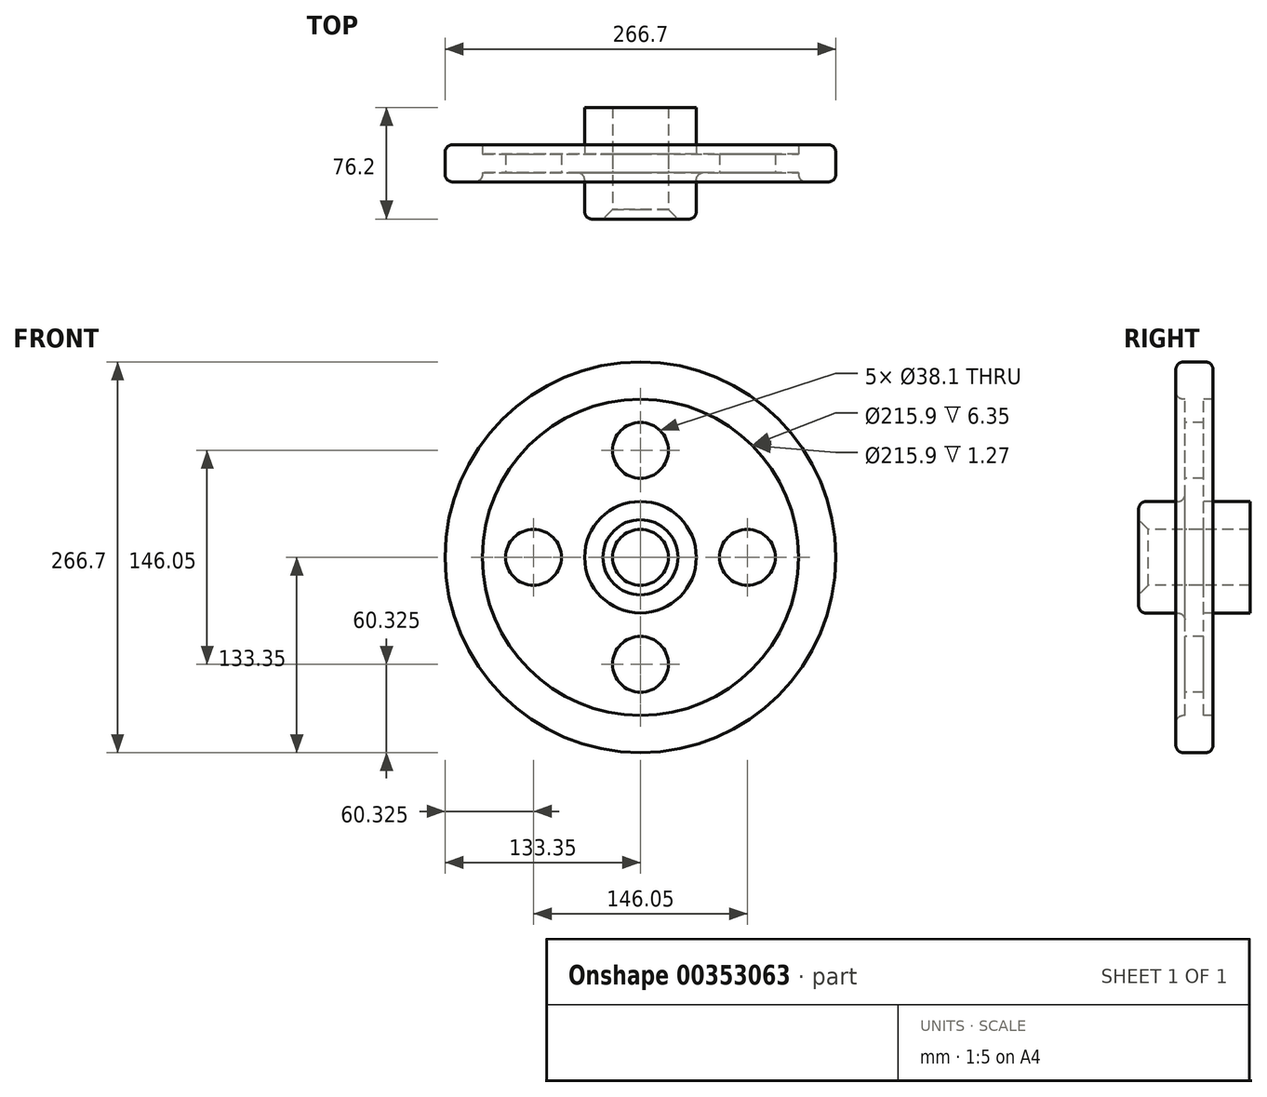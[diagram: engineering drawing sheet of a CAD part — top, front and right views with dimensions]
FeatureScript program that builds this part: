
annotation { "Feature Type Name" : "Feature", "Feature Type Description" : "" }
export const myFeature = defineFeature(function(context is Context, id is Id, definition is map)
    precondition{}
    {
        {
            var Q0;
            Q0=qCreatedBy(makeId("Right.planeOp"),FACE);
            var sketch = newSketch(context, id + "F0", { "sketchPlane" : qUnion([Q0])});
            skLineSegment(sketch, "E0", {"start": v(0, 0) * mm, "end": v(228.48, 0) * mm, "construction": true});
            skLineSegment(sketch, "E1", {"start": v(0, 0) * mm, "end": v(0, 368.94) * mm, "construction": true});
            skLineSegment(sketch, "E2.0", {"start": v(38.1, 19.05) * mm, "end": v(38.1, 38.1) * mm});
            skLineSegment(sketch, "E3.0", {"start": v(0, 19.05) * mm, "end": v(38.1, 19.05) * mm});
            skLineSegment(sketch, "E4.0", {"start": v(6.35, 38.1) * mm, "end": v(38.1, 38.1) * mm});
            skLineSegment(sketch, "E5.0", {"start": v(6.35, 107.95) * mm, "end": v(12.7, 107.95) * mm});
            skLineSegment(sketch, "E6.0", {"start": v(0, 133.35) * mm, "end": v(12.7, 133.35) * mm});
            skLineSegment(sketch, "E7.trimOffspring", {"start": v(12.7, 107.95) * mm, "end": v(12.7, 133.35) * mm});
            skLineSegment(sketch, "E8.trimOffspring", {"start": v(6.35, 38.1) * mm, "end": v(6.35, 107.95) * mm});
            skLineSegment(sketch, "E9.MirrorCS", {"start": v(0, 133.35) * mm, "end": v(-12.7, 133.35) * mm});
            skLineSegment(sketch, "E10.MirrorCS", {"start": v(-12.7, 107.95) * mm, "end": v(-12.7, 133.35) * mm});
            skLineSegment(sketch, "E11.MirrorCS", {"start": v(-6.35, 107.95) * mm, "end": v(-12.7, 107.95) * mm});
            skLineSegment(sketch, "E12.MirrorCS", {"start": v(-6.35, 38.1) * mm, "end": v(-6.35, 107.95) * mm});
            skLineSegment(sketch, "E13.MirrorCS", {"start": v(-6.35, 38.1) * mm, "end": v(-38.1, 38.1) * mm});
            skLineSegment(sketch, "E14.MirrorCS", {"start": v(0, 19.05) * mm, "end": v(-38.1, 19.05) * mm});
            skLineSegment(sketch, "E15.MirrorCS", {"start": v(-38.1, 19.05) * mm, "end": v(-38.1, 38.1) * mm});
            skSolve(sketch);
        }
        {
            var Q0;
            Q0=makeQuery(id+"F0.imprint","IMPRINT",FACE,{"disambiguationData":[TD([[makeQuery(id+"F0.imprint","IMPRINT",EDGE,{"derivedFrom":sQuery(id+"F0.wireOp",EDGE,"E2.0")}),1.0]])]});
            var Q1;
            Q1=sQuery(id+"F0.wireOp",EDGE,"E0");
            revolve(context, id + "F1", {"entities" : qUnion([Q0]), "axis" : qUnion([Q1]), "revolveType" : RevolveType.FULL});
        }
        {
            var Q0;
            Q0=makeQuery(id+"F1.opRevolve","SWEPT_FACE",FACE,{"disambiguationData":[OSD([sQuery(id+"F0.wireOp",EDGE,"E12.MirrorCS")])]});
            var sketch = newSketch(context, id + "F2", { "sketchPlane" : qUnion([Q0])});
            skLineSegment(sketch, "E16", {"start": v(0, 0) * mm, "end": v(0, 73.03) * mm});
            skCircle(sketch, "E17", {"center": v(0, 73.03) * mm, "radius": 19.05 * mm});
            skCircle(sketch, "E18.1.0", {"center": v(-73.03, 0) * mm, "radius": 19.05 * mm});
            skCircle(sketch, "E18.2.0", {"center": v(0, -73.03) * mm, "radius": 19.05 * mm});
            skCircle(sketch, "E18.3.0", {"center": v(73.03, 0) * mm, "radius": 19.05 * mm});
            skPoint(sketch, "E18.center", {"position": v(0, 0) * mm});
            skSolve(sketch);
        }
        {
            var Q0;
            Q0=makeQuery(id+"F2.imprint","IMPRINT",FACE,{"disambiguationData":[TD([[makeQuery(id+"F2.imprint","IMPRINT",EDGE,{"derivedFrom":sQuery(id+"F2.wireOp",EDGE,"E18.2.0")}),1.0]])]});
            var Q1;
            Q1=makeQuery(id+"F2.imprint","IMPRINT",FACE,{"disambiguationData":[TD([[makeQuery(id+"F2.imprint","IMPRINT",EDGE,{"derivedFrom":sQuery(id+"F2.wireOp",EDGE,"E18.3.0")}),1.0]])]});
            var Q2;
            Q2=makeQuery(id+"F2.imprint","IMPRINT",FACE,{"disambiguationData":[TD([[makeQuery(id+"F2.imprint","IMPRINT",EDGE,{"derivedFrom":sQuery(id+"F2.wireOp",EDGE,"E18.1.0")}),1.0]])]});
            var Q3;
            Q3=makeQuery(id+"F2.imprint","IMPRINT",FACE,{"disambiguationData":[TD([[makeQuery(id+"F2.imprint","IMPRINT",EDGE,{"derivedFrom":sQuery(id+"F2.wireOp",EDGE,"E17")}),1.0]])]});
            extrude(context, id + "F3", {"entities" : qUnion([Q0, Q1, Q2, Q3]), "operationType" : NewBodyOperationType.REMOVE, "oppositeDirection" : true, "depth" : 25.4 * mm});
        }
        {
            var Q0;
            Q0=makeQuery(id+"F1.opRevolve","SWEPT_EDGE",EDGE,{"disambiguationData":[OSD([sQuery(id+"F0.wireOp",EDGE,"E12.MirrorCS"),sQuery(id+"F0.wireOp",EDGE,"E13.MirrorCS")])]});
            var Q1;
            Q1=makeQuery(id+"F1.opRevolve","SWEPT_EDGE",EDGE,{"disambiguationData":[OSD([sQuery(id+"F0.wireOp",EDGE,"E13.MirrorCS"),sQuery(id+"F0.wireOp",EDGE,"E15.MirrorCS")])]});
            var Q2;
            Q2=makeQuery(id+"F3.boolean.opBoolean","COPY",EDGE,{"derivedFrom":makeQuery(id+"F3.opExtrude","CAP_EDGE",EDGE,{"disambiguationData":[OSD([sQuery(id+"F2.wireOp",EDGE,"E17")])],"isStart":true})});
            var Q3;
            Q3=makeQuery(id+"F1.opRevolve","SWEPT_EDGE",EDGE,{"disambiguationData":[OSD([sQuery(id+"F0.wireOp",EDGE,"E10.MirrorCS"),sQuery(id+"F0.wireOp",EDGE,"E11.MirrorCS")])]});
            var Q4;
            Q4=makeQuery(id+"F3.boolean.opBoolean","COPY",EDGE,{"derivedFrom":makeQuery(id+"F3.opExtrude","CAP_EDGE",EDGE,{"disambiguationData":[OSD([sQuery(id+"F2.wireOp",EDGE,"E18.2.0")])],"isStart":true})});
            var Q5;
            Q5=makeQuery(id+"F3.boolean.opBoolean","COPY",EDGE,{"derivedFrom":makeQuery(id+"F3.opExtrude","CAP_EDGE",EDGE,{"disambiguationData":[OSD([sQuery(id+"F2.wireOp",EDGE,"E18.3.0")])],"isStart":true})});
            var Q6;
            Q6=makeQuery(id+"F1.opRevolve","SWEPT_EDGE",EDGE,{"disambiguationData":[OSD([sQuery(id+"F0.wireOp",EDGE,"E9.MirrorCS"),sQuery(id+"F0.wireOp",EDGE,"E10.MirrorCS")])]});
            var Q7;
            Q7=makeQuery(id+"F1.opRevolve","SWEPT_EDGE",EDGE,{"disambiguationData":[OSD([sQuery(id+"F0.wireOp",EDGE,"E6.0"),sQuery(id+"F0.wireOp",EDGE,"E7.trimOffspring")])]});
            var Q8;
            Q8=makeQuery(id+"F1.opRevolve","SWEPT_FACE",FACE,{"disambiguationData":[OSD([sQuery(id+"F0.wireOp",EDGE,"E13.MirrorCS")])]});
            fillet(context, id + "F4", {"entities" : qUnion([Q0, Q1, Q2, Q3, Q4, Q5, Q6, Q7, Q8]), "radius" : 5.08 * mm, "tangentPropagation" : true, "allowEdgeOverflow" : false});
        }
        {
            var Q0;
            Q0=makeQuery(id+"F1.opRevolve","SWEPT_EDGE",EDGE,{"disambiguationData":[OSD([sQuery(id+"F0.wireOp",EDGE,"E14.MirrorCS"),sQuery(id+"F0.wireOp",EDGE,"E15.MirrorCS")])]});
            chamfer(context, id + "F5", {"entities" : qUnion([Q0]), "width" : 6.6 * mm, "tangentPropagation" : true});
        }
    });
